# Revit family: CONTURA II PULL OUT SINK MIXER LF
name_source: partatom
category: Plumbing Fixtures
units: mm (PartAtom-declared; Revit-internal decimal feet)

## family parameters
Cut with Voids When Loaded = Yes
Host = Face
OmniClass Number = 23.45.55.17
OmniClass Title = Mixing Faucets
Part Type = Normal
Room Calculation Point = No
Round Connector Dimension = Use Diameter
Shared = No

## types (5) — shared parameters
Assembly Code = D2020300
CW Connection = Yes
HW Connection = Yes
Manufacturer = GWA Bathrooms & Kitchens
URL = https://www.caroma.com.au
Vent Connection = No
Waste Connection = No
zero-valued in all types: Default Elevation

## per-type parameters (varying)
| type | Base_Material | Model |
| CONTURA II PULL OUT SINK MIXER LF - CHROME | GWA_Metal-Chrome | 849062C56AF |
| CONTURA II PULL OUT SINK MIXER LF - MATTE BLACK | GWA-Metal-Black | 849062B56AF |
| CONTURA II PULL OUT SINK MIXER LF - BRUSHED BRASS | GWA_Metal-Brushed-Brass | 849062BB56AF |
| CONTURA II PULL OUT SINK MIXER LF - BRUSHED BRONZE | GWA_Metal-Brushed-Bronze | 849062BBZ56AF |
| CONTURA II PULL OUT SINK MIXER LF - BRUSHED NICKEL | GWA_Metal-Brushed-Nickel | 849062BN56AF |

note: column(s) folded — value = type name in every type: Description

## geometry (parser evidence)
native form markers: Sweep x2
no freeform markers — native parametric forms only
